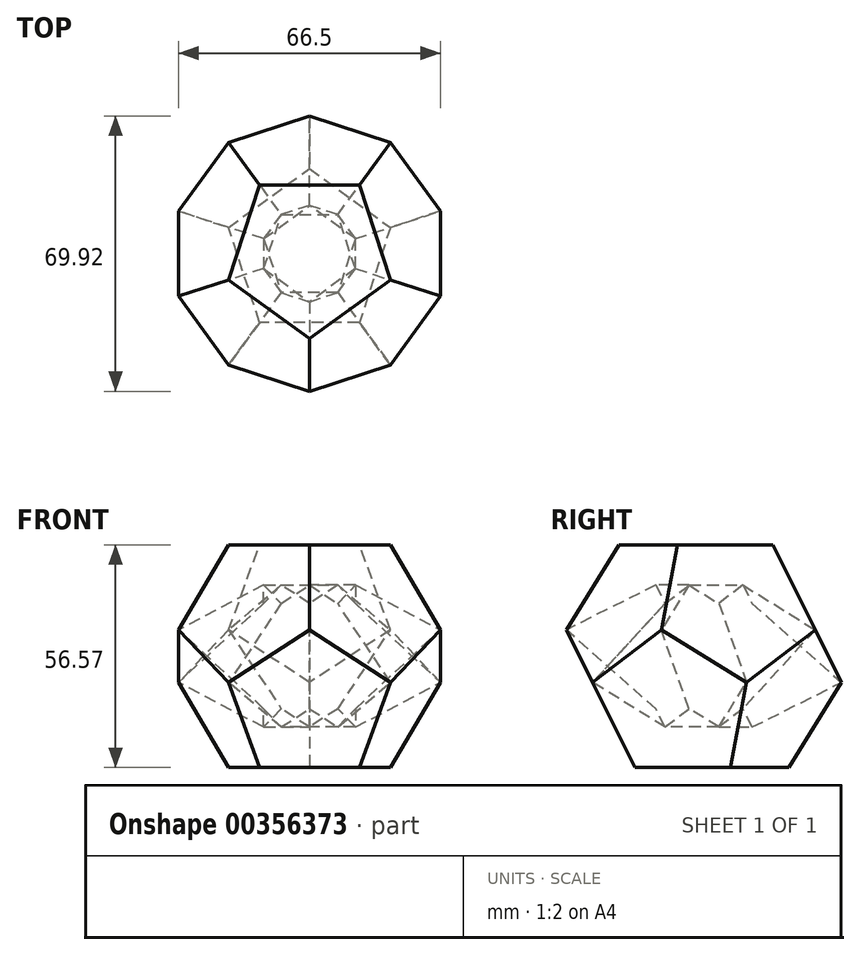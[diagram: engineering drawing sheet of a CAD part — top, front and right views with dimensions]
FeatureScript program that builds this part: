
annotation { "Feature Type Name" : "Feature", "Feature Type Description" : "" }
export const myFeature = defineFeature(function(context is Context, id is Id, definition is map)
    precondition{}
    {
        {
            var Q0;
            Q0=qCreatedBy(makeId("Top.planeOp"),FACE);
            var sketch = newSketch(context, id + "F0", { "sketchPlane" : qUnion([Q0])});
            skCircle(sketch, "E0.cCircle", {"center": v(0, 0) * mm, "radius": 17.48 * mm, "construction": true});
            skLineSegment(sketch, "E0.0", {"start": v(12.7, -17.48) * mm, "end": v(-12.7, -17.48) * mm});
            skLineSegment(sketch, "E0.1", {"start": v(-12.7, -17.48) * mm, "end": v(-20.55, 6.68) * mm});
            skLineSegment(sketch, "E0.2", {"start": v(-20.55, 6.68) * mm, "end": v(0, 21.6) * mm});
            skLineSegment(sketch, "E0.3", {"start": v(0, 21.6) * mm, "end": v(20.55, 6.68) * mm});
            skLineSegment(sketch, "E0.4", {"start": v(20.55, 6.68) * mm, "end": v(12.7, -17.48) * mm});
            skPoint(sketch, "E0.0.midPoint", {"position": v(0, -17.48) * mm});
            skSolve(sketch);
        }
        {
            var Q0;
            Q0=makeQuery(id+"F0.imprint","IMPRINT",FACE,{"disambiguationData":[TD([[makeQuery(id+"F0.imprint","IMPRINT",EDGE,{"derivedFrom":sQuery(id+"F0.wireOp",EDGE,"E0.0")}),-1.0]])]});
            extrude(context, id + "F1", {"entities" : qUnion([Q0]), "depth" : 12.7 * mm, "offsetDistance" : 25.4 * mm, "hasDraft" : true, "draftAngle" : 26.57 * degree});
        }
        {
            var Q0;
            Q0=makeQuery(id+"F1.opExtrude","SWEPT_FACE",FACE,{"disambiguationData":[OSD([sQuery(id+"F0.wireOp",EDGE,"E0.4")])]});
            var sketch = newSketch(context, id + "F2", { "sketchPlane" : qUnion([Q0])});
            skCircle(sketch, "E1.cCircle", {"center": v(-3.64, 25.03) * mm, "radius": 17.48 * mm, "construction": true});
            skLineSegment(sketch, "E1.0", {"start": v(11.44, 9.56) * mm, "end": v(-13.7, 5.9) * mm});
            skLineSegment(sketch, "E1.1", {"start": v(-13.7, 5.9) * mm, "end": v(-24.93, 28.69) * mm});
            skLineSegment(sketch, "E1.2", {"start": v(-24.93, 28.69) * mm, "end": v(-6.74, 46.42) * mm});
            skLineSegment(sketch, "E1.3", {"start": v(-6.74, 46.42) * mm, "end": v(15.74, 34.6) * mm});
            skLineSegment(sketch, "E1.4", {"start": v(15.74, 34.6) * mm, "end": v(11.44, 9.56) * mm});
            skPoint(sketch, "E1.0.midPoint", {"position": v(-1.12, 7.74) * mm});
            skSolve(sketch);
        }
        {
            var Q0;
            Q0 = qSketchRegion(id + "F2", true);
            extrude(context, id + "F3", {"entities" : qUnion([Q0]), "operationType" : NewBodyOperationType.ADD, "oppositeDirection" : true, "depth" : 25.4 * mm, "offsetDistance" : 25.4 * mm});
        }
        {
            var Q0;
            Q0=makeQuery(id+"F1.opExtrude","SWEPT_FACE",FACE,{"disambiguationData":[OSD([sQuery(id+"F0.wireOp",EDGE,"E0.3")])]});
            var sketch = newSketch(context, id + "F4", { "sketchPlane" : qUnion([Q0])});
            skCircle(sketch, "E2.cCircle", {"center": v(-7.82, 24.06) * mm, "radius": 17.48 * mm, "construction": true});
            skLineSegment(sketch, "E2.0", {"start": v(9.66, 11.36) * mm, "end": v(-14.5, 3.51) * mm});
            skLineSegment(sketch, "E2.1", {"start": v(-14.5, 3.51) * mm, "end": v(-29.42, 24.06) * mm});
            skLineSegment(sketch, "E2.2", {"start": v(-29.42, 24.06) * mm, "end": v(-14.5, 44.6) * mm});
            skLineSegment(sketch, "E2.3", {"start": v(-14.5, 44.6) * mm, "end": v(9.66, 36.76) * mm});
            skLineSegment(sketch, "E2.4", {"start": v(9.66, 36.76) * mm, "end": v(9.66, 11.36) * mm});
            skPoint(sketch, "E2.0.midPoint", {"position": v(-2.42, 7.43) * mm});
            skSolve(sketch);
        }
        {
            var Q0;
            Q0 = qSketchRegion(id + "F4", true);
            extrude(context, id + "F5", {"entities" : qUnion([Q0]), "operationType" : NewBodyOperationType.ADD, "oppositeDirection" : true, "depth" : 25.4 * mm, "offsetDistance" : 25.4 * mm});
        }
        {
            var Q0;
            Q0=makeQuery(id+"F1.opExtrude","SWEPT_FACE",FACE,{"disambiguationData":[OSD([sQuery(id+"F0.wireOp",EDGE,"E0.2")])]});
            var sketch = newSketch(context, id + "F6", { "sketchPlane" : qUnion([Q0])});
            skCircle(sketch, "E3.cCircle", {"center": v(7.82, 24.06) * mm, "radius": 17.48 * mm, "construction": true});
            skLineSegment(sketch, "E3.0", {"start": v(14.5, 3.51) * mm, "end": v(-9.66, 11.36) * mm});
            skLineSegment(sketch, "E3.1", {"start": v(-9.66, 11.36) * mm, "end": v(-9.66, 36.76) * mm});
            skLineSegment(sketch, "E3.2", {"start": v(-9.66, 36.76) * mm, "end": v(14.5, 44.6) * mm});
            skLineSegment(sketch, "E3.3", {"start": v(14.5, 44.6) * mm, "end": v(29.42, 24.06) * mm});
            skLineSegment(sketch, "E3.4", {"start": v(29.42, 24.06) * mm, "end": v(14.5, 3.51) * mm});
            skPoint(sketch, "E3.0.midPoint", {"position": v(2.42, 7.43) * mm});
            skSolve(sketch);
        }
        {
            var Q0;
            Q0 = qSketchRegion(id + "F6", true);
            extrude(context, id + "F7", {"entities" : qUnion([Q0]), "operationType" : NewBodyOperationType.ADD, "oppositeDirection" : true, "depth" : 25.4 * mm, "offsetDistance" : 25.4 * mm});
        }
        {
            var Q0;
            Q0=makeQuery(id+"F1.opExtrude","SWEPT_FACE",FACE,{"disambiguationData":[OSD([sQuery(id+"F0.wireOp",EDGE,"E0.1")])]});
            var sketch = newSketch(context, id + "F8", { "sketchPlane" : qUnion([Q0])});
            skCircle(sketch, "E4.cCircle", {"center": v(3.64, 25.03) * mm, "radius": 17.48 * mm, "construction": true});
            skLineSegment(sketch, "E4.0", {"start": v(13.7, 5.9) * mm, "end": v(-11.44, 9.56) * mm});
            skLineSegment(sketch, "E4.1", {"start": v(-11.44, 9.56) * mm, "end": v(-15.74, 34.6) * mm});
            skLineSegment(sketch, "E4.2", {"start": v(-15.74, 34.6) * mm, "end": v(6.74, 46.42) * mm});
            skLineSegment(sketch, "E4.3", {"start": v(6.74, 46.42) * mm, "end": v(24.93, 28.69) * mm});
            skLineSegment(sketch, "E4.4", {"start": v(24.93, 28.69) * mm, "end": v(13.7, 5.9) * mm});
            skPoint(sketch, "E4.0.midPoint", {"position": v(1.12, 7.74) * mm});
            skSolve(sketch);
        }
        {
            var Q0;
            Q0 = qSketchRegion(id + "F8", true);
            extrude(context, id + "F9", {"entities" : qUnion([Q0]), "operationType" : NewBodyOperationType.ADD, "oppositeDirection" : true, "depth" : 25.4 * mm, "offsetDistance" : 25.4 * mm});
        }
        {
            var Q0;
            Q0=makeQuery(id+"F1.opExtrude","SWEPT_FACE",FACE,{"disambiguationData":[OSD([sQuery(id+"F0.wireOp",EDGE,"E0.0")])]});
            var sketch = newSketch(context, id + "F10", { "sketchPlane" : qUnion([Q0])});
            skCircle(sketch, "E5.cCircle", {"center": v(0, 25.3) * mm, "radius": 17.48 * mm, "construction": true});
            skLineSegment(sketch, "E5.0", {"start": v(12.7, 7.82) * mm, "end": v(-12.7, 7.82) * mm});
            skLineSegment(sketch, "E5.1", {"start": v(-12.7, 7.82) * mm, "end": v(-20.55, 31.97) * mm});
            skLineSegment(sketch, "E5.2", {"start": v(-20.55, 31.97) * mm, "end": v(0, 46.9) * mm});
            skLineSegment(sketch, "E5.3", {"start": v(0, 46.9) * mm, "end": v(20.55, 31.97) * mm});
            skLineSegment(sketch, "E5.4", {"start": v(20.55, 31.97) * mm, "end": v(12.7, 7.82) * mm});
            skPoint(sketch, "E5.0.midPoint", {"position": v(0, 7.82) * mm});
            skSolve(sketch);
        }
        {
            var Q0;
            Q0 = qSketchRegion(id + "F10", true);
            extrude(context, id + "F11", {"entities" : qUnion([Q0]), "operationType" : NewBodyOperationType.ADD, "oppositeDirection" : true, "depth" : 25.4 * mm, "offsetDistance" : 25.4 * mm});
        }
        {
            var Q0;
            {var subQ0=sQuery(id+"F4.wireOp",EDGE,"E2.3");var subQ2=sQuery(id+"F6.wireOp",EDGE,"E3.2");var subQ3=sQuery(id+"F6.wireOp",EDGE,"E3.4");var subQ4=sQuery(id+"F6.wireOp",EDGE,"E3.3");var subQ5=makeQuery(id+"F7.opExtrude","CAP_FACE",FACE,{"disambiguationData":[OSD([sQuery(id+"F6.wireOp",EDGE,"E3.0"),sQuery(id+"F6.wireOp",EDGE,"E3.1"),subQ2,subQ4,subQ3])],"isStart":false});Q0=makeQuery(id+"F7.boolean.opBoolean","SPLIT",FACE,{"disambiguationData":[TD([makeQuery(id+"F5.opExtrude","SWEPT_FACE",FACE,{"disambiguationData":[OSD([subQ0])]})])],"derivedFrom":subQ5});}
            var Q1;
            {var subQ0=sQuery(id+"F10.wireOp",EDGE,"E5.2");var subQ1=sQuery(id+"F2.wireOp",EDGE,"E1.2");var subQ2=makeQuery(id+"F3.opExtrude","SWEPT_FACE",FACE,{"disambiguationData":[OSD([subQ1])]});var subQ3=sQuery(id+"F2.wireOp",EDGE,"E1.1");var subQ4=makeQuery(id+"F3.opExtrude","CAP_FACE",FACE,{"disambiguationData":[OSD([sQuery(id+"F2.wireOp",EDGE,"E1.0"),subQ3,subQ1,sQuery(id+"F2.wireOp",EDGE,"E1.3"),sQuery(id+"F2.wireOp",EDGE,"E1.4")])],"isStart":false});var subQ5=sQuery(id+"F8.wireOp",EDGE,"E4.4");var subQ6=sQuery(id+"F8.wireOp",EDGE,"E4.3");var subQ7=sQuery(id+"F8.wireOp",EDGE,"E4.2");var subQ8=sQuery(id+"F8.wireOp",EDGE,"E4.1");var subQ9=sQuery(id+"F8.wireOp",EDGE,"E4.0");var subQ10=makeQuery(id+"F9.opExtrude","CAP_FACE",FACE,{"disambiguationData":[OSD([subQ9,subQ8,subQ7,subQ6,subQ5])],"isStart":false});var subQ11=makeQuery(id+"F9.opExtrude","SWEPT_FACE",FACE,{"disambiguationData":[OSD([subQ7])]});var subQ12=makeQuery(id+"F9.opExtrude","SWEPT_FACE",FACE,{"disambiguationData":[OSD([subQ6])]});var subQ13=sQuery(id+"F6.wireOp",EDGE,"E3.3");Q1=makeQuery(id+"F11.boolean.opBoolean","INTERSECT",VERTEX,{"derivedFrom":[makeQuery(id+"F9.boolean.opBoolean","SPLIT",FACE,{"disambiguationData":[TD([makeQuery(id+"F7.opExtrude","SWEPT_FACE",FACE,{"disambiguationData":[OSD([subQ13])]})])],"derivedFrom":subQ10}),makeQuery(id+"F9.boolean.opBoolean","SPLIT",FACE,{"disambiguationData":[TD([makeQuery(id+"F1.opExtrude","SWEPT_FACE",FACE,{"disambiguationData":[OSD([sQuery(id+"F0.wireOp",EDGE,"E0.1")])]}),subQ4,makeQuery(id+"F3.opExtrude","SWEPT_FACE",FACE,{"disambiguationData":[OSD([subQ3])]}),subQ2,makeQuery(id+"F9.opExtrude","CAP_FACE",FACE,{"disambiguationData":[OSD([subQ9,subQ8,subQ7,subQ6,subQ5])],"isStart":true}),subQ10,subQ11,subQ12,makeQuery(id+"F9.opExtrude","SWEPT_FACE",FACE,{"disambiguationData":[OSD([subQ5])]})])],"derivedFrom":subQ12}),makeQuery(id+"F11.opExtrude","CAP_FACE",FACE,{"disambiguationData":[OSD([sQuery(id+"F10.wireOp",EDGE,"E5.0"),sQuery(id+"F10.wireOp",EDGE,"E5.1"),subQ0,sQuery(id+"F10.wireOp",EDGE,"E5.3"),sQuery(id+"F10.wireOp",EDGE,"E5.4")])],"isStart":false}),makeQuery(id+"F11.opExtrude","SWEPT_FACE",FACE,{"disambiguationData":[OSD([subQ0])]})]});}
            loft(context, id + "F12", {"operationType" : NewBodyOperationType.ADD, "sheetProfilesArray" : [{ "sheetProfileEntities" : qUnion([Q0]) }, { "sheetProfileEntities" : qUnion([Q1]) }]});
        }
        {
            var Q0;
            Q0=makeQuery(id+"F5.opExtrude","CAP_FACE",FACE,{"disambiguationData":[OSD([sQuery(id+"F4.wireOp",EDGE,"E2.0"),sQuery(id+"F4.wireOp",EDGE,"E2.1"),sQuery(id+"F4.wireOp",EDGE,"E2.2"),sQuery(id+"F4.wireOp",EDGE,"E2.3"),sQuery(id+"F4.wireOp",EDGE,"E2.4")])],"isStart":false});
            var Q1;
            {var subQ0=sQuery(id+"F10.wireOp",EDGE,"E5.4");var subQ1=sQuery(id+"F10.wireOp",EDGE,"E5.3");var subQ2=sQuery(id+"F10.wireOp",EDGE,"E5.2");var subQ3=sQuery(id+"F10.wireOp",EDGE,"E5.1");var subQ4=sQuery(id+"F10.wireOp",EDGE,"E5.0");var subQ5=sQuery(id+"F8.wireOp",EDGE,"E4.4");var subQ6=sQuery(id+"F8.wireOp",EDGE,"E4.3");var subQ7=sQuery(id+"F8.wireOp",EDGE,"E4.2");var subQ8=sQuery(id+"F8.wireOp",EDGE,"E4.1");var subQ9=sQuery(id+"F8.wireOp",EDGE,"E4.0");var subQ10=sQuery(id+"F6.wireOp",EDGE,"E3.4");var subQ11=sQuery(id+"F6.wireOp",EDGE,"E3.3");var subQ12=sQuery(id+"F6.wireOp",EDGE,"E3.2");var subQ13=sQuery(id+"F6.wireOp",EDGE,"E3.1");var subQ14=sQuery(id+"F6.wireOp",EDGE,"E3.0");var subQ15=sQuery(id+"F2.wireOp",EDGE,"E1.2");var subQ16=makeQuery(id+"F3.opExtrude","SWEPT_FACE",FACE,{"disambiguationData":[OSD([subQ15])]});var subQ17=sQuery(id+"F2.wireOp",EDGE,"E1.1");var subQ18=makeQuery(id+"F3.opExtrude","CAP_FACE",FACE,{"disambiguationData":[OSD([sQuery(id+"F2.wireOp",EDGE,"E1.0"),subQ17,subQ15,sQuery(id+"F2.wireOp",EDGE,"E1.3"),sQuery(id+"F2.wireOp",EDGE,"E1.4")])],"isStart":false});var subQ19=makeQuery(id+"F9.opExtrude","CAP_FACE",FACE,{"disambiguationData":[OSD([subQ9,subQ8,subQ7,subQ6,subQ5])],"isStart":false});var subQ20=makeQuery(id+"F9.opExtrude","SWEPT_FACE",FACE,{"disambiguationData":[OSD([subQ7])]});var subQ21=makeQuery(id+"F9.opExtrude","SWEPT_FACE",FACE,{"disambiguationData":[OSD([subQ6])]});Q1=makeQuery(id+"F12.boolean.opBoolean","MERGE",VERTEX,{"derivedFrom":[makeQuery(id+"F11.boolean.opBoolean","INTERSECT",VERTEX,{"derivedFrom":[makeQuery(id+"F9.boolean.opBoolean","SPLIT",FACE,{"disambiguationData":[TD([makeQuery(id+"F7.opExtrude","SWEPT_FACE",FACE,{"disambiguationData":[OSD([subQ11])]})])],"derivedFrom":subQ19}),makeQuery(id+"F9.boolean.opBoolean","SPLIT",FACE,{"disambiguationData":[TD([makeQuery(id+"F1.opExtrude","SWEPT_FACE",FACE,{"disambiguationData":[OSD([sQuery(id+"F0.wireOp",EDGE,"E0.1")])]}),subQ18,makeQuery(id+"F3.opExtrude","SWEPT_FACE",FACE,{"disambiguationData":[OSD([subQ17])]}),subQ16,makeQuery(id+"F9.opExtrude","CAP_FACE",FACE,{"disambiguationData":[OSD([subQ9,subQ8,subQ7,subQ6,subQ5])],"isStart":true}),subQ19,subQ20,subQ21,makeQuery(id+"F9.opExtrude","SWEPT_FACE",FACE,{"disambiguationData":[OSD([subQ5])]})])],"derivedFrom":subQ21}),makeQuery(id+"F11.opExtrude","CAP_FACE",FACE,{"disambiguationData":[OSD([subQ4,subQ3,subQ2,subQ1,subQ0])],"isStart":false}),makeQuery(id+"F11.opExtrude","SWEPT_FACE",FACE,{"disambiguationData":[OSD([subQ2])]})]}),makeQuery(id+"F12.opLoft","SWEPT_VERTEX",VERTEX,{"disambiguationData":[OSD([subQ14,subQ13,subQ12,subQ11,subQ10,subQ9,subQ8,subQ7,subQ6,subQ5,subQ4,subQ3,subQ2,subQ1,subQ0])]})]});}
            loft(context, id + "F13", {"operationType" : NewBodyOperationType.ADD, "sheetProfilesArray" : [{ "sheetProfileEntities" : qUnion([Q0]) }, { "sheetProfileEntities" : qUnion([Q1]) }]});
        }
        {
            var Q0;
            {var subQ2=sQuery(id+"F2.wireOp",EDGE,"E1.3");var subQ3=makeQuery(id+"F3.opExtrude","SWEPT_FACE",FACE,{"disambiguationData":[OSD([subQ2])]});var subQ4=sQuery(id+"F2.wireOp",EDGE,"E1.2");var subQ5=makeQuery(id+"F3.opExtrude","SWEPT_FACE",FACE,{"disambiguationData":[OSD([subQ4])]});var subQ6=sQuery(id+"F2.wireOp",EDGE,"E1.1");var subQ7=makeQuery(id+"F3.opExtrude","CAP_FACE",FACE,{"disambiguationData":[OSD([sQuery(id+"F2.wireOp",EDGE,"E1.0"),subQ6,subQ4,subQ2,sQuery(id+"F2.wireOp",EDGE,"E1.4")])],"isStart":false});Q0=makeQuery(id+"F9.boolean.opBoolean","SPLIT",FACE,{"disambiguationData":[TD([subQ3])],"derivedFrom":makeQuery(id+"F7.boolean.opBoolean","SPLIT",FACE,{"disambiguationData":[TD([subQ5])],"derivedFrom":subQ7})});}
            var Q1;
            {var subQ0=sQuery(id+"F10.wireOp",EDGE,"E5.4");var subQ1=sQuery(id+"F10.wireOp",EDGE,"E5.3");var subQ2=sQuery(id+"F10.wireOp",EDGE,"E5.2");var subQ3=sQuery(id+"F10.wireOp",EDGE,"E5.1");var subQ4=sQuery(id+"F10.wireOp",EDGE,"E5.0");var subQ5=sQuery(id+"F8.wireOp",EDGE,"E4.4");var subQ6=sQuery(id+"F8.wireOp",EDGE,"E4.3");var subQ7=sQuery(id+"F8.wireOp",EDGE,"E4.2");var subQ8=sQuery(id+"F8.wireOp",EDGE,"E4.1");var subQ9=sQuery(id+"F8.wireOp",EDGE,"E4.0");var subQ10=sQuery(id+"F6.wireOp",EDGE,"E3.4");var subQ11=sQuery(id+"F6.wireOp",EDGE,"E3.3");var subQ12=sQuery(id+"F6.wireOp",EDGE,"E3.2");var subQ13=sQuery(id+"F6.wireOp",EDGE,"E3.1");var subQ14=sQuery(id+"F6.wireOp",EDGE,"E3.0");var subQ15=sQuery(id+"F4.wireOp",EDGE,"E2.4");var subQ16=sQuery(id+"F4.wireOp",EDGE,"E2.3");var subQ17=sQuery(id+"F4.wireOp",EDGE,"E2.2");var subQ18=sQuery(id+"F4.wireOp",EDGE,"E2.1");var subQ19=sQuery(id+"F4.wireOp",EDGE,"E2.0");var subQ20=sQuery(id+"F2.wireOp",EDGE,"E1.2");var subQ21=makeQuery(id+"F3.opExtrude","SWEPT_FACE",FACE,{"disambiguationData":[OSD([subQ20])]});var subQ22=sQuery(id+"F2.wireOp",EDGE,"E1.1");var subQ23=makeQuery(id+"F3.opExtrude","CAP_FACE",FACE,{"disambiguationData":[OSD([sQuery(id+"F2.wireOp",EDGE,"E1.0"),subQ22,subQ20,sQuery(id+"F2.wireOp",EDGE,"E1.3"),sQuery(id+"F2.wireOp",EDGE,"E1.4")])],"isStart":false});var subQ24=makeQuery(id+"F9.opExtrude","CAP_FACE",FACE,{"disambiguationData":[OSD([subQ9,subQ8,subQ7,subQ6,subQ5])],"isStart":false});var subQ25=makeQuery(id+"F9.opExtrude","SWEPT_FACE",FACE,{"disambiguationData":[OSD([subQ7])]});var subQ26=makeQuery(id+"F9.opExtrude","SWEPT_FACE",FACE,{"disambiguationData":[OSD([subQ6])]});Q1=makeQuery(id+"F13.boolean.opBoolean","MERGE",VERTEX,{"derivedFrom":[makeQuery(id+"F12.boolean.opBoolean","MERGE",VERTEX,{"derivedFrom":[makeQuery(id+"F11.boolean.opBoolean","INTERSECT",VERTEX,{"derivedFrom":[makeQuery(id+"F9.boolean.opBoolean","SPLIT",FACE,{"disambiguationData":[TD([makeQuery(id+"F7.opExtrude","SWEPT_FACE",FACE,{"disambiguationData":[OSD([subQ11])]})])],"derivedFrom":subQ24}),makeQuery(id+"F9.boolean.opBoolean","SPLIT",FACE,{"disambiguationData":[TD([makeQuery(id+"F1.opExtrude","SWEPT_FACE",FACE,{"disambiguationData":[OSD([sQuery(id+"F0.wireOp",EDGE,"E0.1")])]}),subQ23,makeQuery(id+"F3.opExtrude","SWEPT_FACE",FACE,{"disambiguationData":[OSD([subQ22])]}),subQ21,makeQuery(id+"F9.opExtrude","CAP_FACE",FACE,{"disambiguationData":[OSD([subQ9,subQ8,subQ7,subQ6,subQ5])],"isStart":true}),subQ24,subQ25,subQ26,makeQuery(id+"F9.opExtrude","SWEPT_FACE",FACE,{"disambiguationData":[OSD([subQ5])]})])],"derivedFrom":subQ26}),makeQuery(id+"F11.opExtrude","CAP_FACE",FACE,{"disambiguationData":[OSD([subQ4,subQ3,subQ2,subQ1,subQ0])],"isStart":false}),makeQuery(id+"F11.opExtrude","SWEPT_FACE",FACE,{"disambiguationData":[OSD([subQ2])]})]}),makeQuery(id+"F12.opLoft","SWEPT_VERTEX",VERTEX,{"disambiguationData":[OSD([subQ14,subQ13,subQ12,subQ11,subQ10,subQ9,subQ8,subQ7,subQ6,subQ5,subQ4,subQ3,subQ2,subQ1,subQ0])]})]}),makeQuery(id+"F13.opLoft","SWEPT_VERTEX",VERTEX,{"disambiguationData":[OSD([subQ19,subQ18,subQ17,subQ16,subQ15,subQ14,subQ13,subQ12,subQ11,subQ10,subQ9,subQ8,subQ7,subQ6,subQ5,subQ4,subQ3,subQ2,subQ1,subQ0])]})]});}
            loft(context, id + "F14", {"operationType" : NewBodyOperationType.ADD, "sheetProfilesArray" : [{ "sheetProfileEntities" : qUnion([Q0]) }, { "sheetProfileEntities" : qUnion([Q1]) }]});
        }
        {
            var Q0;
            Q0=makeQuery(id+"F9.opExtrude","CAP_VERTEX",VERTEX,{"disambiguationData":[OSD([sQuery(id+"F8.wireOp",EDGE,"E4.2"),sQuery(id+"F8.wireOp",EDGE,"E4.3")])],"isStart":false});
            var Q1;
            Q1=makeQuery(id+"F12.opLoft","SWEPT_FACE",FACE,{"disambiguationData":[OSD([sQuery(id+"F6.wireOp",EDGE,"E3.0"),sQuery(id+"F6.wireOp",EDGE,"E3.1"),sQuery(id+"F6.wireOp",EDGE,"E3.2"),sQuery(id+"F6.wireOp",EDGE,"E3.3"),sQuery(id+"F6.wireOp",EDGE,"E3.4"),sQuery(id+"F8.wireOp",EDGE,"E4.0"),sQuery(id+"F8.wireOp",EDGE,"E4.1"),sQuery(id+"F8.wireOp",EDGE,"E4.2"),sQuery(id+"F8.wireOp",EDGE,"E4.3"),sQuery(id+"F8.wireOp",EDGE,"E4.4")])]});
            loft(context, id + "F15", {"operationType" : NewBodyOperationType.ADD, "sheetProfilesArray" : [{ "sheetProfileEntities" : qUnion([Q0]) }, { "sheetProfileEntities" : qUnion([Q1]) }]});
        }
        {
            var Q0;
            {var subQ0=sQuery(id+"F10.wireOp",EDGE,"E5.4");var subQ1=sQuery(id+"F10.wireOp",EDGE,"E5.3");var subQ2=sQuery(id+"F10.wireOp",EDGE,"E5.2");var subQ3=sQuery(id+"F10.wireOp",EDGE,"E5.1");var subQ4=sQuery(id+"F10.wireOp",EDGE,"E5.0");var subQ5=sQuery(id+"F8.wireOp",EDGE,"E4.4");var subQ6=sQuery(id+"F8.wireOp",EDGE,"E4.3");var subQ7=sQuery(id+"F8.wireOp",EDGE,"E4.2");var subQ8=sQuery(id+"F8.wireOp",EDGE,"E4.1");var subQ9=sQuery(id+"F8.wireOp",EDGE,"E4.0");var subQ10=sQuery(id+"F6.wireOp",EDGE,"E3.4");var subQ11=sQuery(id+"F6.wireOp",EDGE,"E3.3");var subQ12=sQuery(id+"F6.wireOp",EDGE,"E3.2");var subQ13=sQuery(id+"F6.wireOp",EDGE,"E3.1");var subQ14=sQuery(id+"F6.wireOp",EDGE,"E3.0");var subQ15=sQuery(id+"F4.wireOp",EDGE,"E2.4");var subQ16=sQuery(id+"F4.wireOp",EDGE,"E2.3");var subQ17=sQuery(id+"F4.wireOp",EDGE,"E2.2");var subQ18=sQuery(id+"F4.wireOp",EDGE,"E2.1");var subQ19=sQuery(id+"F4.wireOp",EDGE,"E2.0");var subQ20=sQuery(id+"F2.wireOp",EDGE,"E1.4");var subQ21=sQuery(id+"F2.wireOp",EDGE,"E1.3");var subQ22=sQuery(id+"F2.wireOp",EDGE,"E1.2");var subQ23=sQuery(id+"F2.wireOp",EDGE,"E1.1");var subQ24=sQuery(id+"F2.wireOp",EDGE,"E1.0");var subQ25=makeQuery(id+"F3.opExtrude","SWEPT_FACE",FACE,{"disambiguationData":[OSD([subQ22])]});var subQ26=makeQuery(id+"F3.opExtrude","CAP_FACE",FACE,{"disambiguationData":[OSD([subQ24,subQ23,subQ22,subQ21,subQ20])],"isStart":false});var subQ27=makeQuery(id+"F9.opExtrude","CAP_FACE",FACE,{"disambiguationData":[OSD([subQ9,subQ8,subQ7,subQ6,subQ5])],"isStart":false});var subQ28=makeQuery(id+"F9.opExtrude","SWEPT_FACE",FACE,{"disambiguationData":[OSD([subQ7])]});var subQ29=makeQuery(id+"F9.opExtrude","SWEPT_FACE",FACE,{"disambiguationData":[OSD([subQ6])]});Q0=makeQuery(id+"F15.boolean.opBoolean","MERGE",FACE,{"derivedFrom":[makeQuery(id+"F12.opLoft","SWEPT_FACE",FACE,{"disambiguationData":[OSD([subQ19,subQ18,subQ17,subQ16,subQ15,subQ14,subQ13,subQ12,subQ11,subQ10])]}),makeQuery(id+"F15.opLoft","SWEPT_FACE",FACE,{"disambiguationData":[OSD([subQ24,subQ23,subQ22,subQ21,subQ20,subQ19,subQ18,subQ17,subQ16,subQ15,subQ14,subQ13,subQ12,subQ11,subQ10,subQ9,subQ8,subQ7,subQ6,subQ5,subQ4,subQ3,subQ2,subQ1,subQ0]),TDD([makeQuery(id+"F12.opLoft","SWEPT_EDGE",EDGE,{"disambiguationData":[OSD([subQ12,subQ11,subQ9,subQ8,subQ7,subQ6,subQ5,subQ4,subQ3,subQ2,subQ1,subQ0])]}),makeQuery(id+"F12.boolean.opBoolean","MERGE",VERTEX,{"derivedFrom":[makeQuery(id+"F7.opExtrude","CAP_VERTEX",VERTEX,{"disambiguationData":[OSD([subQ12,subQ11])],"isStart":false}),makeQuery(id+"F12.opLoft","MID_CAP_VERTEX",VERTEX,{"disambiguationData":[OSD([subQ12,subQ11])],"capPos":0.0})]}),makeQuery(id+"F14.boolean.opBoolean","MERGE",VERTEX,{"derivedFrom":[makeQuery(id+"F13.boolean.opBoolean","MERGE",VERTEX,{"derivedFrom":[makeQuery(id+"F12.boolean.opBoolean","MERGE",VERTEX,{"derivedFrom":[makeQuery(id+"F11.boolean.opBoolean","INTERSECT",VERTEX,{"derivedFrom":[makeQuery(id+"F9.boolean.opBoolean","SPLIT",FACE,{"disambiguationData":[TD([makeQuery(id+"F7.opExtrude","SWEPT_FACE",FACE,{"disambiguationData":[OSD([subQ11])]})])],"derivedFrom":subQ27}),makeQuery(id+"F9.boolean.opBoolean","SPLIT",FACE,{"disambiguationData":[TD([makeQuery(id+"F1.opExtrude","SWEPT_FACE",FACE,{"disambiguationData":[OSD([sQuery(id+"F0.wireOp",EDGE,"E0.1")])]}),subQ26,makeQuery(id+"F3.opExtrude","SWEPT_FACE",FACE,{"disambiguationData":[OSD([subQ23])]}),subQ25,makeQuery(id+"F9.opExtrude","CAP_FACE",FACE,{"disambiguationData":[OSD([subQ9,subQ8,subQ7,subQ6,subQ5])],"isStart":true}),subQ27,subQ28,subQ29,makeQuery(id+"F9.opExtrude","SWEPT_FACE",FACE,{"disambiguationData":[OSD([subQ5])]})])],"derivedFrom":subQ29}),makeQuery(id+"F11.opExtrude","CAP_FACE",FACE,{"disambiguationData":[OSD([subQ4,subQ3,subQ2,subQ1,subQ0])],"isStart":false}),makeQuery(id+"F11.opExtrude","SWEPT_FACE",FACE,{"disambiguationData":[OSD([subQ2])]})]}),makeQuery(id+"F12.opLoft","SWEPT_VERTEX",VERTEX,{"disambiguationData":[OSD([subQ14,subQ13,subQ12,subQ11,subQ10,subQ9,subQ8,subQ7,subQ6,subQ5,subQ4,subQ3,subQ2,subQ1,subQ0])]})]}),makeQuery(id+"F13.opLoft","SWEPT_VERTEX",VERTEX,{"disambiguationData":[OSD([subQ19,subQ18,subQ17,subQ16,subQ15,subQ14,subQ13,subQ12,subQ11,subQ10,subQ9,subQ8,subQ7,subQ6,subQ5,subQ4,subQ3,subQ2,subQ1,subQ0])]})]}),makeQuery(id+"F14.opLoft","SWEPT_VERTEX",VERTEX,{"disambiguationData":[OSD([subQ24,subQ23,subQ22,subQ21,subQ20,subQ19,subQ18,subQ17,subQ16,subQ15,subQ14,subQ13,subQ12,subQ11,subQ10,subQ9,subQ8,subQ7,subQ6,subQ5,subQ4,subQ3,subQ2,subQ1,subQ0])]})]})])]})]});}
            var Q1;
            {var subQ0=sQuery(id+"F4.wireOp",EDGE,"E2.3");var subQ1=sQuery(id+"F4.wireOp",EDGE,"E2.2");Q1=makeQuery(id+"F13.boolean.opBoolean","MERGE",VERTEX,{"derivedFrom":[makeQuery(id+"F5.opExtrude","CAP_VERTEX",VERTEX,{"disambiguationData":[OSD([subQ1,subQ0])],"isStart":false}),makeQuery(id+"F13.opLoft","MID_CAP_VERTEX",VERTEX,{"disambiguationData":[OSD([subQ1,subQ0])],"capPos":0.0})]});}
            loft(context, id + "F16", {"operationType" : NewBodyOperationType.ADD, "sheetProfilesArray" : [{ "sheetProfileEntities" : qUnion([Q0]) }, { "sheetProfileEntities" : qUnion([Q1]) }]});
        }
        {
            var Q0;
            {var subQ0=sQuery(id+"F2.wireOp",EDGE,"E1.3");var subQ1=sQuery(id+"F2.wireOp",EDGE,"E1.2");Q0=makeQuery(id+"F14.boolean.opBoolean","MERGE",VERTEX,{"derivedFrom":[makeQuery(id+"F3.opExtrude","CAP_VERTEX",VERTEX,{"disambiguationData":[OSD([subQ1,subQ0])],"isStart":false}),makeQuery(id+"F14.opLoft","MID_CAP_VERTEX",VERTEX,{"disambiguationData":[OSD([subQ1,subQ0])],"capPos":0.0})]});}
            var Q1;
            {var subQ0=sQuery(id+"F10.wireOp",EDGE,"E5.4");var subQ1=sQuery(id+"F10.wireOp",EDGE,"E5.3");var subQ2=sQuery(id+"F10.wireOp",EDGE,"E5.2");var subQ3=sQuery(id+"F10.wireOp",EDGE,"E5.1");var subQ4=sQuery(id+"F10.wireOp",EDGE,"E5.0");var subQ5=sQuery(id+"F8.wireOp",EDGE,"E4.4");var subQ6=sQuery(id+"F8.wireOp",EDGE,"E4.3");var subQ7=sQuery(id+"F8.wireOp",EDGE,"E4.2");var subQ8=sQuery(id+"F8.wireOp",EDGE,"E4.1");var subQ9=sQuery(id+"F8.wireOp",EDGE,"E4.0");var subQ10=sQuery(id+"F6.wireOp",EDGE,"E3.4");var subQ11=sQuery(id+"F6.wireOp",EDGE,"E3.3");var subQ12=sQuery(id+"F6.wireOp",EDGE,"E3.2");var subQ13=sQuery(id+"F6.wireOp",EDGE,"E3.1");var subQ14=sQuery(id+"F6.wireOp",EDGE,"E3.0");var subQ15=sQuery(id+"F4.wireOp",EDGE,"E2.4");var subQ16=sQuery(id+"F4.wireOp",EDGE,"E2.3");var subQ17=sQuery(id+"F4.wireOp",EDGE,"E2.2");var subQ18=sQuery(id+"F4.wireOp",EDGE,"E2.1");var subQ19=sQuery(id+"F4.wireOp",EDGE,"E2.0");var subQ20=sQuery(id+"F2.wireOp",EDGE,"E1.4");var subQ21=sQuery(id+"F2.wireOp",EDGE,"E1.3");var subQ22=sQuery(id+"F2.wireOp",EDGE,"E1.2");var subQ23=sQuery(id+"F2.wireOp",EDGE,"E1.1");var subQ24=sQuery(id+"F2.wireOp",EDGE,"E1.0");var subQ25=makeQuery(id+"F9.opExtrude","SWEPT_FACE",FACE,{"disambiguationData":[OSD([subQ7])]});var subQ26=makeQuery(id+"F9.opExtrude","CAP_FACE",FACE,{"disambiguationData":[OSD([subQ9,subQ8,subQ7,subQ6,subQ5])],"isStart":false});var subQ27=makeQuery(id+"F3.opExtrude","SWEPT_FACE",FACE,{"disambiguationData":[OSD([subQ22])]});var subQ28=makeQuery(id+"F3.opExtrude","CAP_FACE",FACE,{"disambiguationData":[OSD([subQ24,subQ23,subQ22,subQ21,subQ20])],"isStart":false});var subQ29=makeQuery(id+"F9.opExtrude","SWEPT_FACE",FACE,{"disambiguationData":[OSD([subQ6])]});Q1=makeQuery(id+"F16.boolean.opBoolean","MERGE",FACE,{"derivedFrom":[makeQuery(id+"F13.opLoft","SWEPT_FACE",FACE,{"disambiguationData":[OSD([subQ24,subQ23,subQ22,subQ21,subQ20,subQ19,subQ18,subQ17,subQ16,subQ15])]}),makeQuery(id+"F16.opLoft","SWEPT_FACE",FACE,{"disambiguationData":[OSD([subQ24,subQ23,subQ22,subQ21,subQ20,subQ19,subQ18,subQ17,subQ16,subQ15,subQ14,subQ13,subQ12,subQ11,subQ10,subQ9,subQ8,subQ7,subQ6,subQ5,subQ4,subQ3,subQ2,subQ1,subQ0]),TDD([makeQuery(id+"F15.boolean.opBoolean","MERGE",VERTEX,{"derivedFrom":[makeQuery(id+"F9.opExtrude","CAP_VERTEX",VERTEX,{"disambiguationData":[OSD([subQ7,subQ6])],"isStart":false}),makeQuery(id+"F15.opLoft","SWEPT_VERTEX",VERTEX,{"disambiguationData":[OSD([subQ12,subQ11,subQ7,subQ6])]})]}),makeQuery(id+"F15.boolean.opBoolean","MERGE",VERTEX,{"derivedFrom":[makeQuery(id+"F14.boolean.opBoolean","MERGE",VERTEX,{"derivedFrom":[makeQuery(id+"F13.boolean.opBoolean","MERGE",VERTEX,{"derivedFrom":[makeQuery(id+"F12.boolean.opBoolean","MERGE",VERTEX,{"derivedFrom":[makeQuery(id+"F11.boolean.opBoolean","INTERSECT",VERTEX,{"derivedFrom":[makeQuery(id+"F9.boolean.opBoolean","SPLIT",FACE,{"disambiguationData":[TD([makeQuery(id+"F7.opExtrude","SWEPT_FACE",FACE,{"disambiguationData":[OSD([subQ11])]})])],"derivedFrom":subQ26}),makeQuery(id+"F9.boolean.opBoolean","SPLIT",FACE,{"disambiguationData":[TD([makeQuery(id+"F1.opExtrude","SWEPT_FACE",FACE,{"disambiguationData":[OSD([sQuery(id+"F0.wireOp",EDGE,"E0.1")])]}),subQ28,makeQuery(id+"F3.opExtrude","SWEPT_FACE",FACE,{"disambiguationData":[OSD([subQ23])]}),subQ27,makeQuery(id+"F9.opExtrude","CAP_FACE",FACE,{"disambiguationData":[OSD([subQ9,subQ8,subQ7,subQ6,subQ5])],"isStart":true}),subQ26,subQ25,subQ29,makeQuery(id+"F9.opExtrude","SWEPT_FACE",FACE,{"disambiguationData":[OSD([subQ5])]})])],"derivedFrom":subQ29}),makeQuery(id+"F11.opExtrude","CAP_FACE",FACE,{"disambiguationData":[OSD([subQ4,subQ3,subQ2,subQ1,subQ0])],"isStart":false}),makeQuery(id+"F11.opExtrude","SWEPT_FACE",FACE,{"disambiguationData":[OSD([subQ2])]})]}),makeQuery(id+"F12.opLoft","SWEPT_VERTEX",VERTEX,{"disambiguationData":[OSD([subQ14,subQ13,subQ12,subQ11,subQ10,subQ9,subQ8,subQ7,subQ6,subQ5,subQ4,subQ3,subQ2,subQ1,subQ0])]})]}),makeQuery(id+"F13.opLoft","SWEPT_VERTEX",VERTEX,{"disambiguationData":[OSD([subQ19,subQ18,subQ17,subQ16,subQ15,subQ14,subQ13,subQ12,subQ11,subQ10,subQ9,subQ8,subQ7,subQ6,subQ5,subQ4,subQ3,subQ2,subQ1,subQ0])]})]}),makeQuery(id+"F14.opLoft","SWEPT_VERTEX",VERTEX,{"disambiguationData":[OSD([subQ24,subQ23,subQ22,subQ21,subQ20,subQ19,subQ18,subQ17,subQ16,subQ15,subQ14,subQ13,subQ12,subQ11,subQ10,subQ9,subQ8,subQ7,subQ6,subQ5,subQ4,subQ3,subQ2,subQ1,subQ0])]})]}),makeQuery(id+"F15.opLoft","MID_CAP_VERTEX",VERTEX,{"disambiguationData":[OSD([subQ24,subQ23,subQ22,subQ21,subQ20,subQ19,subQ18,subQ17,subQ16,subQ15,subQ14,subQ13,subQ12,subQ11,subQ10,subQ9,subQ8,subQ7,subQ6,subQ5,subQ4,subQ3,subQ2,subQ1,subQ0])],"capPos":1.0})]}),makeQuery(id+"F15.boolean.opBoolean","MERGE",EDGE,{"derivedFrom":[makeQuery(id+"F9.boolean.opBoolean","SPLIT",EDGE,{"disambiguationData":[TD([subQ25])],"derivedFrom":makeQuery(id+"F9.opExtrude","CAP_EDGE",EDGE,{"disambiguationData":[OSD([subQ6])],"isStart":false})}),makeQuery(id+"F15.opLoft","SWEPT_EDGE",EDGE,{"disambiguationData":[OSD([subQ24,subQ23,subQ22,subQ21,subQ20,subQ19,subQ18,subQ17,subQ16,subQ15,subQ14,subQ13,subQ12,subQ11,subQ10,subQ9,subQ8,subQ7,subQ6,subQ5,subQ4,subQ3,subQ2,subQ1,subQ0])]})]})])]})]});}
            loft(context, id + "F17", {"operationType" : NewBodyOperationType.ADD, "sheetProfilesArray" : [{ "sheetProfileEntities" : qUnion([Q0]) }, { "sheetProfileEntities" : qUnion([Q1]) }]});
        }
        {
            var Q0;
            {var subQ0=sQuery(id+"F10.wireOp",EDGE,"E5.4");var subQ1=sQuery(id+"F10.wireOp",EDGE,"E5.3");var subQ2=sQuery(id+"F10.wireOp",EDGE,"E5.2");var subQ3=sQuery(id+"F10.wireOp",EDGE,"E5.1");var subQ4=sQuery(id+"F10.wireOp",EDGE,"E5.0");var subQ5=sQuery(id+"F8.wireOp",EDGE,"E4.4");var subQ6=sQuery(id+"F8.wireOp",EDGE,"E4.3");var subQ7=sQuery(id+"F8.wireOp",EDGE,"E4.2");var subQ8=sQuery(id+"F8.wireOp",EDGE,"E4.1");var subQ9=sQuery(id+"F8.wireOp",EDGE,"E4.0");var subQ10=sQuery(id+"F6.wireOp",EDGE,"E3.4");var subQ11=sQuery(id+"F6.wireOp",EDGE,"E3.3");var subQ12=sQuery(id+"F6.wireOp",EDGE,"E3.2");var subQ13=sQuery(id+"F6.wireOp",EDGE,"E3.1");var subQ14=sQuery(id+"F6.wireOp",EDGE,"E3.0");var subQ15=sQuery(id+"F4.wireOp",EDGE,"E2.4");var subQ16=sQuery(id+"F4.wireOp",EDGE,"E2.3");var subQ17=sQuery(id+"F4.wireOp",EDGE,"E2.2");var subQ18=sQuery(id+"F4.wireOp",EDGE,"E2.1");var subQ19=sQuery(id+"F4.wireOp",EDGE,"E2.0");var subQ20=sQuery(id+"F2.wireOp",EDGE,"E1.4");var subQ21=sQuery(id+"F2.wireOp",EDGE,"E1.3");var subQ22=sQuery(id+"F2.wireOp",EDGE,"E1.2");var subQ23=sQuery(id+"F2.wireOp",EDGE,"E1.1");var subQ24=sQuery(id+"F2.wireOp",EDGE,"E1.0");var subQ25=makeQuery(id+"F9.opExtrude","SWEPT_FACE",FACE,{"disambiguationData":[OSD([subQ7])]});var subQ26=makeQuery(id+"F9.opExtrude","CAP_FACE",FACE,{"disambiguationData":[OSD([subQ9,subQ8,subQ7,subQ6,subQ5])],"isStart":false});var subQ27=makeQuery(id+"F3.opExtrude","SWEPT_FACE",FACE,{"disambiguationData":[OSD([subQ22])]});var subQ28=makeQuery(id+"F3.opExtrude","CAP_FACE",FACE,{"disambiguationData":[OSD([subQ24,subQ23,subQ22,subQ21,subQ20])],"isStart":false});var subQ29=makeQuery(id+"F9.opExtrude","SWEPT_FACE",FACE,{"disambiguationData":[OSD([subQ6])]});var subQ30=makeQuery(id+"F15.boolean.opBoolean","MERGE",EDGE,{"derivedFrom":[makeQuery(id+"F9.boolean.opBoolean","SPLIT",EDGE,{"disambiguationData":[TD([subQ25])],"derivedFrom":makeQuery(id+"F9.opExtrude","CAP_EDGE",EDGE,{"disambiguationData":[OSD([subQ6])],"isStart":false})}),makeQuery(id+"F15.opLoft","SWEPT_EDGE",EDGE,{"disambiguationData":[OSD([subQ24,subQ23,subQ22,subQ21,subQ20,subQ19,subQ18,subQ17,subQ16,subQ15,subQ14,subQ13,subQ12,subQ11,subQ10,subQ9,subQ8,subQ7,subQ6,subQ5,subQ4,subQ3,subQ2,subQ1,subQ0])]})]});var subQ31=makeQuery(id+"F15.boolean.opBoolean","MERGE",VERTEX,{"derivedFrom":[makeQuery(id+"F14.boolean.opBoolean","MERGE",VERTEX,{"derivedFrom":[makeQuery(id+"F13.boolean.opBoolean","MERGE",VERTEX,{"derivedFrom":[makeQuery(id+"F12.boolean.opBoolean","MERGE",VERTEX,{"derivedFrom":[makeQuery(id+"F11.boolean.opBoolean","INTERSECT",VERTEX,{"derivedFrom":[makeQuery(id+"F9.boolean.opBoolean","SPLIT",FACE,{"disambiguationData":[TD([makeQuery(id+"F7.opExtrude","SWEPT_FACE",FACE,{"disambiguationData":[OSD([subQ11])]})])],"derivedFrom":subQ26}),makeQuery(id+"F9.boolean.opBoolean","SPLIT",FACE,{"disambiguationData":[TD([makeQuery(id+"F1.opExtrude","SWEPT_FACE",FACE,{"disambiguationData":[OSD([sQuery(id+"F0.wireOp",EDGE,"E0.1")])]}),subQ28,makeQuery(id+"F3.opExtrude","SWEPT_FACE",FACE,{"disambiguationData":[OSD([subQ23])]}),subQ27,makeQuery(id+"F9.opExtrude","CAP_FACE",FACE,{"disambiguationData":[OSD([subQ9,subQ8,subQ7,subQ6,subQ5])],"isStart":true}),subQ26,subQ25,subQ29,makeQuery(id+"F9.opExtrude","SWEPT_FACE",FACE,{"disambiguationData":[OSD([subQ5])]})])],"derivedFrom":subQ29}),makeQuery(id+"F11.opExtrude","CAP_FACE",FACE,{"disambiguationData":[OSD([subQ4,subQ3,subQ2,subQ1,subQ0])],"isStart":false}),makeQuery(id+"F11.opExtrude","SWEPT_FACE",FACE,{"disambiguationData":[OSD([subQ2])]})]}),makeQuery(id+"F12.opLoft","SWEPT_VERTEX",VERTEX,{"disambiguationData":[OSD([subQ14,subQ13,subQ12,subQ11,subQ10,subQ9,subQ8,subQ7,subQ6,subQ5,subQ4,subQ3,subQ2,subQ1,subQ0])]})]}),makeQuery(id+"F13.opLoft","SWEPT_VERTEX",VERTEX,{"disambiguationData":[OSD([subQ19,subQ18,subQ17,subQ16,subQ15,subQ14,subQ13,subQ12,subQ11,subQ10,subQ9,subQ8,subQ7,subQ6,subQ5,subQ4,subQ3,subQ2,subQ1,subQ0])]})]}),makeQuery(id+"F14.opLoft","SWEPT_VERTEX",VERTEX,{"disambiguationData":[OSD([subQ24,subQ23,subQ22,subQ21,subQ20,subQ19,subQ18,subQ17,subQ16,subQ15,subQ14,subQ13,subQ12,subQ11,subQ10,subQ9,subQ8,subQ7,subQ6,subQ5,subQ4,subQ3,subQ2,subQ1,subQ0])]})]}),makeQuery(id+"F15.opLoft","MID_CAP_VERTEX",VERTEX,{"disambiguationData":[OSD([subQ24,subQ23,subQ22,subQ21,subQ20,subQ19,subQ18,subQ17,subQ16,subQ15,subQ14,subQ13,subQ12,subQ11,subQ10,subQ9,subQ8,subQ7,subQ6,subQ5,subQ4,subQ3,subQ2,subQ1,subQ0])],"capPos":1.0})]});var subQ32=makeQuery(id+"F15.boolean.opBoolean","MERGE",VERTEX,{"derivedFrom":[makeQuery(id+"F9.opExtrude","CAP_VERTEX",VERTEX,{"disambiguationData":[OSD([subQ7,subQ6])],"isStart":false}),makeQuery(id+"F15.opLoft","SWEPT_VERTEX",VERTEX,{"disambiguationData":[OSD([subQ12,subQ11,subQ7,subQ6])]})]});Q0=makeQuery(id+"F17.boolean.opBoolean","MERGE",FACE,{"derivedFrom":[makeQuery(id+"F14.opLoft","SWEPT_FACE",FACE,{"disambiguationData":[OSD([subQ24,subQ23,subQ22,subQ21,subQ20,subQ4,subQ3,subQ2,subQ1,subQ0])]}),makeQuery(id+"F17.opLoft","SWEPT_FACE",FACE,{"disambiguationData":[OSD([subQ24,subQ23,subQ22,subQ21,subQ20,subQ19,subQ18,subQ17,subQ16,subQ15,subQ14,subQ13,subQ12,subQ11,subQ10,subQ9,subQ8,subQ7,subQ6,subQ5,subQ4,subQ3,subQ2,subQ1,subQ0]),TDD([makeQuery(id+"F16.boolean.opBoolean","MERGE",VERTEX,{"derivedFrom":[subQ32,makeQuery(id+"F16.opLoft","MID_CAP_VERTEX",VERTEX,{"disambiguationData":[OSD([subQ12,subQ11,subQ7,subQ6])],"capPos":0.0})]}),makeQuery(id+"F16.boolean.opBoolean","MERGE",VERTEX,{"derivedFrom":[subQ31,makeQuery(id+"F16.opLoft","MID_CAP_VERTEX",VERTEX,{"disambiguationData":[OSD([subQ24,subQ23,subQ22,subQ21,subQ20,subQ19,subQ18,subQ17,subQ16,subQ15,subQ14,subQ13,subQ12,subQ11,subQ10,subQ9,subQ8,subQ7,subQ6,subQ5,subQ4,subQ3,subQ2,subQ1,subQ0])],"capPos":0.0})]}),makeQuery(id+"F16.boolean.opBoolean","MERGE",EDGE,{"derivedFrom":[subQ30,makeQuery(id+"F16.opLoft","MID_CAP_EDGE",EDGE,{"disambiguationData":[OSD([subQ24,subQ23,subQ22,subQ21,subQ20,subQ19,subQ18,subQ17,subQ16,subQ15,subQ14,subQ13,subQ12,subQ11,subQ10,subQ9,subQ8,subQ7,subQ6,subQ5,subQ4,subQ3,subQ2,subQ1,subQ0]),TDD([subQ32,subQ31,subQ30])],"capPos":0.0})]})])]})]});}
            var Q1;
            Q1=makeQuery(id+"F11.opExtrude","CAP_VERTEX",VERTEX,{"disambiguationData":[OSD([sQuery(id+"F10.wireOp",EDGE,"E5.2"),sQuery(id+"F10.wireOp",EDGE,"E5.3")])],"isStart":false});
            loft(context, id + "F18", {"operationType" : NewBodyOperationType.ADD, "sheetProfilesArray" : [{ "sheetProfileEntities" : qUnion([Q0]) }, { "sheetProfileEntities" : qUnion([Q1]) }]});
        }
        {
            var Q0;
            {var subQ0=sQuery(id+"F8.wireOp",EDGE,"E4.3");var subQ1=sQuery(id+"F8.wireOp",EDGE,"E4.2");var subQ2=sQuery(id+"F6.wireOp",EDGE,"E3.3");var subQ3=sQuery(id+"F6.wireOp",EDGE,"E3.2");var subQ4=sQuery(id+"F10.wireOp",EDGE,"E5.4");var subQ5=sQuery(id+"F10.wireOp",EDGE,"E5.3");var subQ6=sQuery(id+"F10.wireOp",EDGE,"E5.2");var subQ7=sQuery(id+"F10.wireOp",EDGE,"E5.1");var subQ8=sQuery(id+"F10.wireOp",EDGE,"E5.0");var subQ9=sQuery(id+"F8.wireOp",EDGE,"E4.4");var subQ10=sQuery(id+"F8.wireOp",EDGE,"E4.1");var subQ11=sQuery(id+"F8.wireOp",EDGE,"E4.0");var subQ12=sQuery(id+"F6.wireOp",EDGE,"E3.4");var subQ13=sQuery(id+"F6.wireOp",EDGE,"E3.1");var subQ14=sQuery(id+"F6.wireOp",EDGE,"E3.0");var subQ15=sQuery(id+"F4.wireOp",EDGE,"E2.4");var subQ16=sQuery(id+"F4.wireOp",EDGE,"E2.3");var subQ17=sQuery(id+"F4.wireOp",EDGE,"E2.2");var subQ18=sQuery(id+"F4.wireOp",EDGE,"E2.1");var subQ19=sQuery(id+"F4.wireOp",EDGE,"E2.0");var subQ20=sQuery(id+"F2.wireOp",EDGE,"E1.4");var subQ21=sQuery(id+"F2.wireOp",EDGE,"E1.3");var subQ22=sQuery(id+"F2.wireOp",EDGE,"E1.2");var subQ23=sQuery(id+"F2.wireOp",EDGE,"E1.1");var subQ24=sQuery(id+"F2.wireOp",EDGE,"E1.0");Q0=makeQuery(id+"F18.boolean.opBoolean","MERGE",FACE,{"derivedFrom":[makeQuery(id+"F17.boolean.opBoolean","MERGE",FACE,{"derivedFrom":[makeQuery(id+"F16.opLoft","SWEPT_FACE",FACE,{"disambiguationData":[OSD([subQ3,subQ2,subQ1,subQ0])]}),makeQuery(id+"F17.opLoft","SWEPT_FACE",FACE,{"disambiguationData":[OSD([subQ17,subQ16,subQ3,subQ2,subQ1,subQ0])]})]}),makeQuery(id+"F18.opLoft","SWEPT_FACE",FACE,{"disambiguationData":[OSD([subQ24,subQ23,subQ22,subQ21,subQ20,subQ19,subQ18,subQ17,subQ16,subQ15,subQ14,subQ13,subQ3,subQ2,subQ12,subQ11,subQ10,subQ1,subQ0,subQ9,subQ8,subQ7,subQ6,subQ5,subQ4]),TDD([makeQuery(id+"F17.opLoft","SWEPT_EDGE",EDGE,{"disambiguationData":[OSD([subQ22,subQ21,subQ3,subQ2,subQ1,subQ0])]}),makeQuery(id+"F17.boolean.opBoolean","MERGE",VERTEX,{"derivedFrom":[makeQuery(id+"F14.boolean.opBoolean","MERGE",VERTEX,{"derivedFrom":[makeQuery(id+"F3.opExtrude","CAP_VERTEX",VERTEX,{"disambiguationData":[OSD([subQ22,subQ21])],"isStart":false}),makeQuery(id+"F14.opLoft","MID_CAP_VERTEX",VERTEX,{"disambiguationData":[OSD([subQ22,subQ21])],"capPos":0.0})]}),makeQuery(id+"F17.opLoft","SWEPT_VERTEX",VERTEX,{"disambiguationData":[OSD([subQ24,subQ23,subQ22,subQ21,subQ20,subQ19,subQ18,subQ17,subQ16,subQ15,subQ14,subQ13,subQ3,subQ2,subQ12,subQ11,subQ10,subQ1,subQ0,subQ9,subQ8,subQ7,subQ6,subQ5,subQ4])]})]}),makeQuery(id+"F17.boolean.opBoolean","MERGE",VERTEX,{"derivedFrom":[makeQuery(id+"F16.boolean.opBoolean","MERGE",VERTEX,{"derivedFrom":[makeQuery(id+"F15.boolean.opBoolean","MERGE",VERTEX,{"derivedFrom":[makeQuery(id+"F9.opExtrude","CAP_VERTEX",VERTEX,{"disambiguationData":[OSD([subQ1,subQ0])],"isStart":false}),makeQuery(id+"F15.opLoft","SWEPT_VERTEX",VERTEX,{"disambiguationData":[OSD([subQ3,subQ2,subQ1,subQ0])]})]}),makeQuery(id+"F16.opLoft","MID_CAP_VERTEX",VERTEX,{"disambiguationData":[OSD([subQ3,subQ2,subQ1,subQ0])],"capPos":0.0})]}),makeQuery(id+"F17.opLoft","MID_CAP_VERTEX",VERTEX,{"disambiguationData":[OSD([subQ3,subQ2,subQ1,subQ0])],"capPos":1.0})]})])]})]});}
            cPlane(context, id + "F19", {"entities" : qUnion([Q0]), "cplaneType" : CPlaneType.OFFSET, "offset" : 25.4 * mm, "width" : 152.4 * mm, "height" : 152.4 * mm});
        }
        {
            var Q0;
            Q0=makeQuery(id+"F1.opExtrude","SWEPT_BODY",BODY,{"disambiguationData":[OSD([sQuery(id+"F0.wireOp",EDGE,"E0.0"),sQuery(id+"F0.wireOp",EDGE,"E0.1"),sQuery(id+"F0.wireOp",EDGE,"E0.2"),sQuery(id+"F0.wireOp",EDGE,"E0.3"),sQuery(id+"F0.wireOp",EDGE,"E0.4")])]});
            var Q1;
            Q1=qCreatedBy(id+"F19.planeOp",FACE);
            mirror(context, id + "F20", {"entities" : qUnion([Q0]), "mirrorPlane" : qUnion([Q1])});
        }
        {
            var Q0;
            Q0=qCreatedBy(makeId("Front.planeOp"),FACE);
            var sketch = newSketch(context, id + "F21", { "sketchPlane" : qUnion([Q0])});
            skLineSegment(sketch, "E6", {"start": v(0, -60.15) * mm, "end": v(0, 75.3) * mm});
            skSolve(sketch);
        }
        {
            var Q0;
            Q0=makeQuery(id+"F20.opPattern","COPY",BODY,{"derivedFrom":makeQuery(id+"F1.opExtrude","SWEPT_BODY",BODY,{"disambiguationData":[OSD([sQuery(id+"F0.wireOp",EDGE,"E0.0"),sQuery(id+"F0.wireOp",EDGE,"E0.1"),sQuery(id+"F0.wireOp",EDGE,"E0.2"),sQuery(id+"F0.wireOp",EDGE,"E0.3"),sQuery(id+"F0.wireOp",EDGE,"E0.4")])]}),"instanceName":"1"});
            var Q1;
            Q1=sQuery(id+"F21.wireOp",EDGE,"E6");
            transform(context, id + "F22", {"entities" : qUnion([Q0]), "transformType" : TransformType.ROTATION, "transformAxis" : qUnion([Q1]), "angle" : 180 * degree, "makeCopy" : false});
        }
        {
            var Q0;
            Q0=makeQuery(id+"F20.opPattern","COPY",BODY,{"derivedFrom":makeQuery(id+"F1.opExtrude","SWEPT_BODY",BODY,{"disambiguationData":[OSD([sQuery(id+"F0.wireOp",EDGE,"E0.0"),sQuery(id+"F0.wireOp",EDGE,"E0.1"),sQuery(id+"F0.wireOp",EDGE,"E0.2"),sQuery(id+"F0.wireOp",EDGE,"E0.3"),sQuery(id+"F0.wireOp",EDGE,"E0.4")])]}),"instanceName":"1"});
            transform(context, id + "F23", {"entities" : qUnion([Q0]), "transformType" : TransformType.TRANSLATION_3D, "dx" : 0 * mm, "dy" : 0 * mm, "dz" : -86.87 * mm, "makeCopy" : false});
        }
    });
